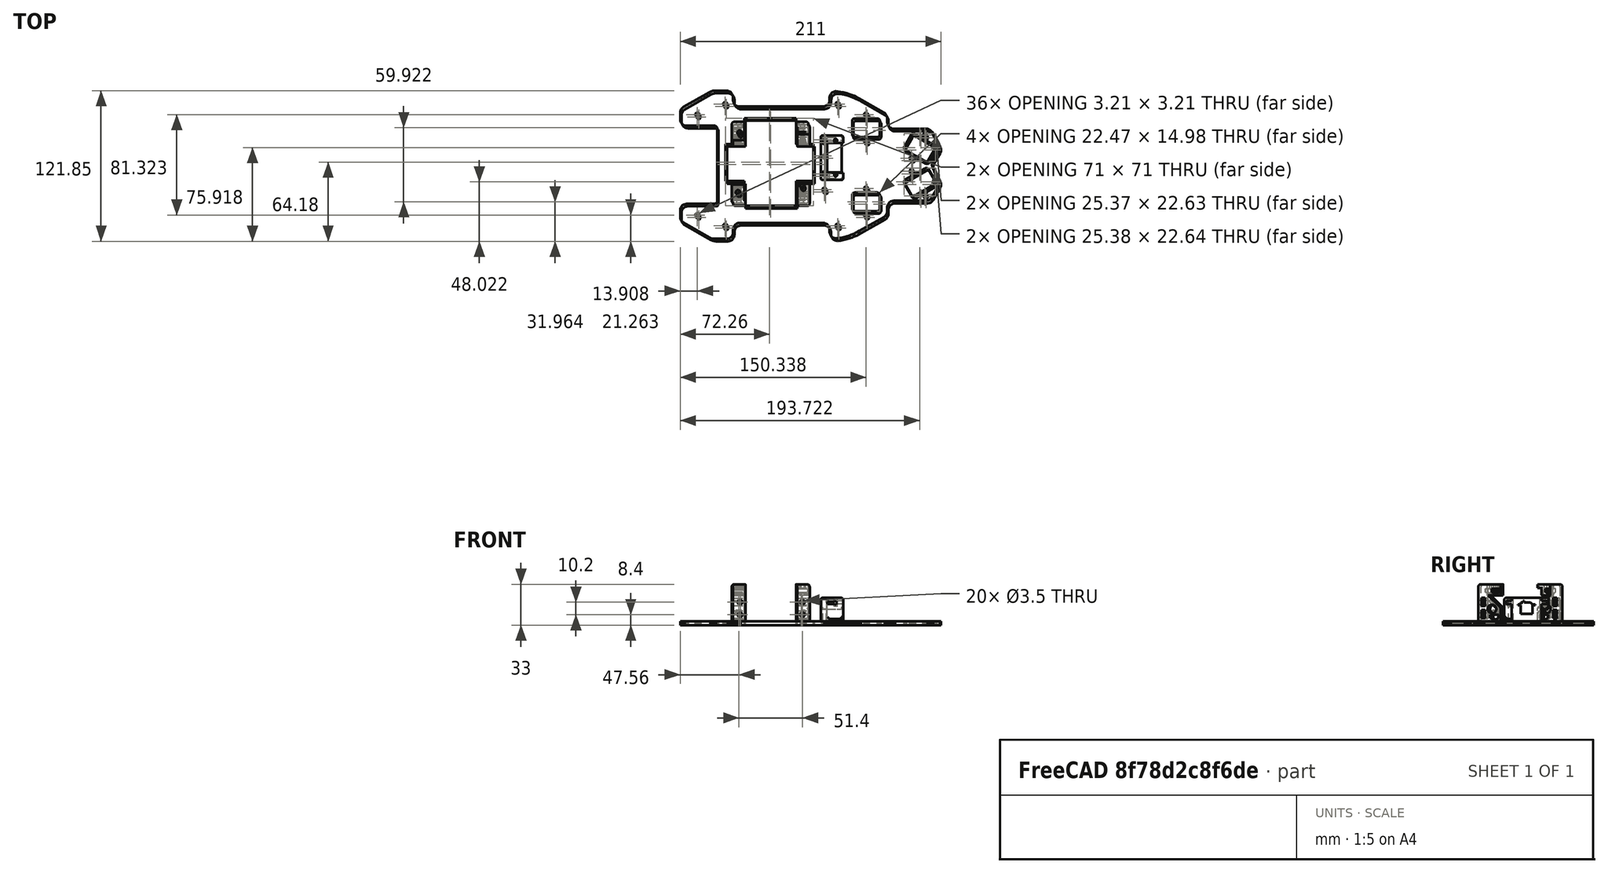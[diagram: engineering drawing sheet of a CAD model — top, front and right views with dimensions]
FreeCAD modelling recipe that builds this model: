
FCSTD DOCUMENT  (FreeCAD 0.16R6698 (Git))
Label: base_v2
License: All rights reserved
LicenseURL: http://es.wikipedia.org/wiki/Todos_los_derechos_reservados
objects: Part::Cut×10, Part::Box×5, Part::Feature×3, Part::Cylinder×2, Mesh::Feature×1, Part::Chamfer×1, Part::MultiFuse×1
note: 22 computed .brp shape members not serialized (recipe doc carries the construction recipe); baked Part::Feature solids carry a one-line shape summary decoded from their .brp

FEATURE [Mesh::Feature] Base_Evolution  label="Base Evolution"
  Placement = pos=(-116,101,-4) rot=(0,0,1;0rad)
FEATURE [Part::Chamfer] Chamfer009  label="CUERPO_FINAL"
  Edges = 30 edges r=0.4: [Edge70,Edge72,Edge74,Edge79,Edge89,Edge92,Edge96,Edge99,Edge101,Edge102,Edge104,Edge106,Edge108,Edge110,Edge112,Edge419,Edge421,Edge424,Edge426,Edge430,Edge432,Edge436,Edge438,Edge441,Edge443,Edge444,Edge446,Edge448,Edge450,Edge455]
FEATURE [Part::Box] Box  label="Cubo"
  Height = 42
  Length = 71
  Placement = pos=(-27,-15,-1) rot=(0,0,1;0rad)
  Width = 30
FEATURE [Part::Box] Box001  label="Cubo001"
  Height = 42
  Length = 42
  Placement = pos=(-12,-35,-1) rot=(0,0,1;0rad)
  Width = 71
FEATURE [Part::Feature] Base_Evolution001
  shape: bbox 210 x 119.8 x 3 mm, 4376 faces, 0 solids (baked)
FEATURE [Part::Cut] Cut
  Base = -> Chamfer009
  Tool = -> Box001
FEATURE [Part::Cut] Cut001
  Base = -> Cut
  Tool = -> Box
FEATURE [Part::Feature] Base_Evolution001_solid  label="Base_Evolution001 (Solid)"
  shape: bbox 210 x 119.8 x 3 mm, 4376 faces (baked)
FEATURE [Part::Cut] Cut002
  Base = -> Base_Evolution001_solid
  Tool = -> Box001
FEATURE [Part::Cut] Cut003
  Base = -> Cut002
  Tool = -> Box
FEATURE [Part::MultiFuse] Fusion  label="base+Cuerpo"
  Shapes = -> [Cut001,Cut003]
FEATURE [Part::Box] Box002  label="Cubo002"
  Height = 10
  Length = 15
  Placement = pos=(27.0941,14.9696,27.4836) rot=(0,0,1;0rad)
  Width = 10
FEATURE [Part::Cut] Cut004
  Base = -> Fusion
  Tool = -> Box002
FEATURE [Part::Feature] Cut004001  label="Cut005"
  shape: bbox 210 x 119.8 x 33 mm, 1321 faces (baked)
FEATURE [Part::Box] Box003  label="Cubo003"
  Height = 10
  Length = 15
  Placement = pos=(-25.4958,-17.7991,28.3813) rot=(0,0,1;0rad)
  Width = 36
FEATURE [Part::Cut] Cut004002  label="Base+Cuerpo Recortada"
  Base = -> Cut004001
  Placement = pos=(-1,2,0) rot=(0,0,1;0rad)
  Tool = -> Box003
FEATURE [Part::Cut] Cut056  label="SUJETA MINISERVO FINAL"
FEATURE [Part::Box] Box004  label="huecoServo"
  Height = 10
  Length = 12
  Placement = pos=(54,-6,-5) rot=(0,0,1;0rad)
  Width = 24
FEATURE [Part::Cut] Cut004003
  Base = -> Cut004002
  Tool = -> Box004
FEATURE [Part::Cylinder] Cylinder  label="Cilindro"
  Angle = 360
  Height = 29
  Placement = pos=(61,-8,-3) rot=(0,0,1;0rad)
  Radius = 1.2
FEATURE [Part::Cut] Cut004004
  Base = -> Cut004003
  Tool = -> Cylinder
FEATURE [Part::Cylinder] Cylinder001  label="Cilindro001"
  Angle = 360
  Height = 29
  Placement = pos=(61,20,-3) rot=(0,0,1;0rad)
  Radius = 1.2
FEATURE [Part::Cut] Cut004005  label="Base v2"
  Base = -> Cut004004
  Tool = -> Cylinder001
